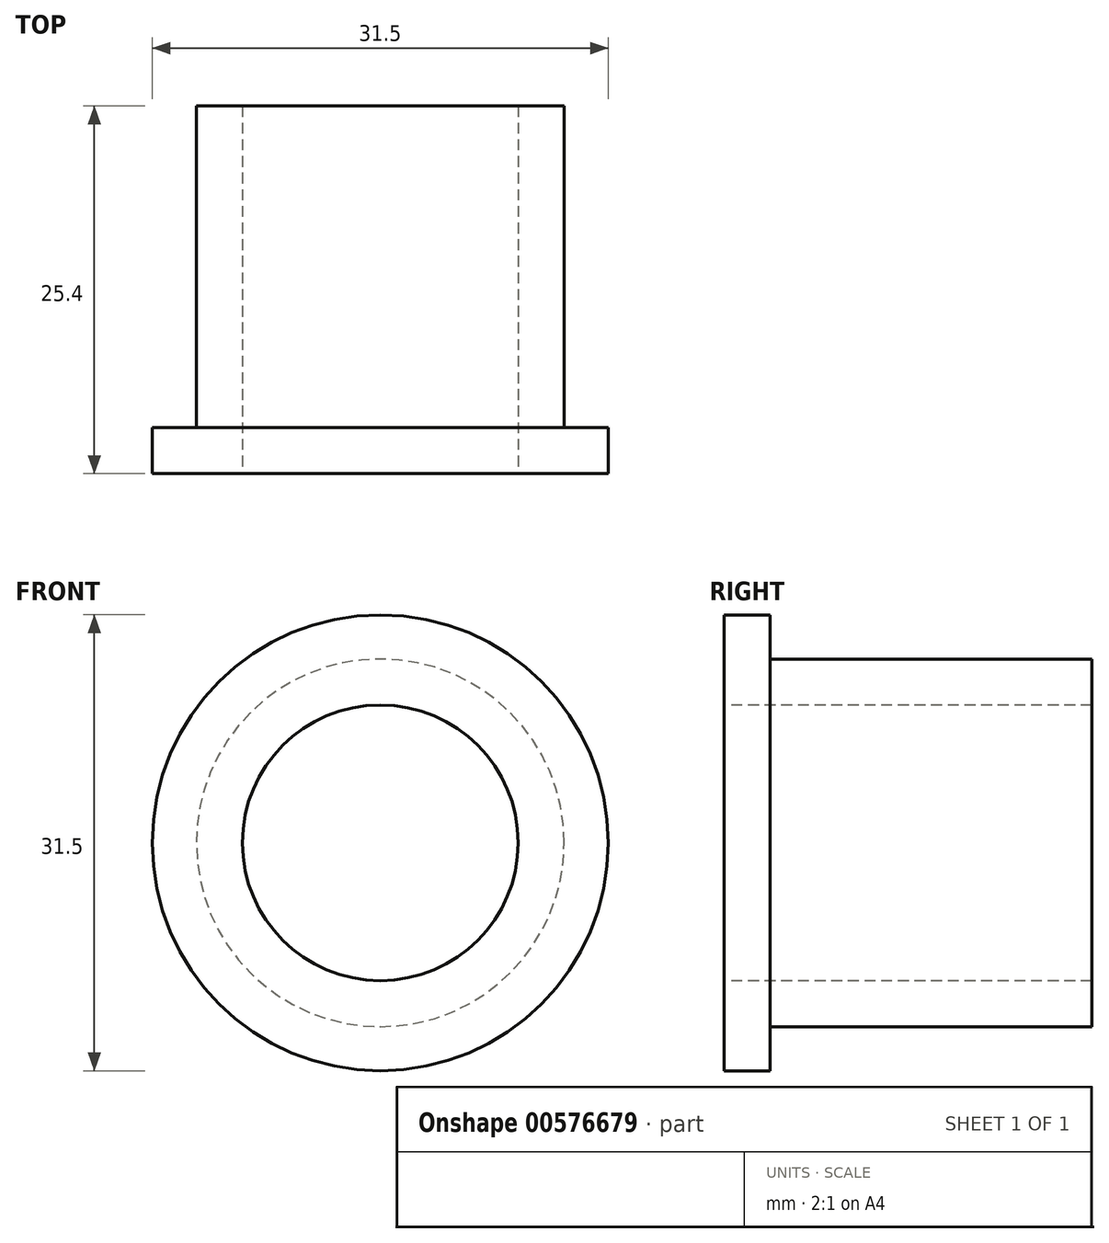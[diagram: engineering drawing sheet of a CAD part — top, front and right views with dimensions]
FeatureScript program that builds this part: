
annotation { "Feature Type Name" : "Feature", "Feature Type Description" : "" }
export const myFeature = defineFeature(function(context is Context, id is Id, definition is map)
    precondition{}
    {
        {
            var Q0;
            Q0=qCreatedBy(makeId("Front.planeOp"),FACE);
            var sketch = newSketch(context, id + "F0", { "sketchPlane" : qUnion([Q0])});
            skCircle(sketch, "E0", {"center": v(0, 0) * mm, "radius": 15.75 * mm});
            skCircle(sketch, "E1", {"center": v(0, 0) * mm, "radius": 12.7 * mm});
            skSolve(sketch);
        }
        {
            var Q0;
            Q0=makeQuery(id+"F0.imprint","IMPRINT",FACE,{"disambiguationData":[TD([[makeQuery(id+"F0.imprint","IMPRINT",EDGE,{"derivedFrom":sQuery(id+"F0.wireOp",EDGE,"E0")}),1.0]])]});
            var Q1;
            Q1=makeQuery(id+"F0.imprint","IMPRINT",FACE,{"disambiguationData":[TD([[makeQuery(id+"F0.imprint","IMPRINT",EDGE,{"derivedFrom":sQuery(id+"F0.wireOp",EDGE,"E1")}),1.0]])]});
            extrude(context, id + "F1", {"entities" : qUnion([Q0, Q1]), "depth" : -3.17 * mm, "offsetDistance" : 25.4 * mm});
        }
        {
            var Q0;
            Q0=makeQuery(id+"F0.imprint","IMPRINT",FACE,{"disambiguationData":[TD([[makeQuery(id+"F0.imprint","IMPRINT",EDGE,{"derivedFrom":sQuery(id+"F0.wireOp",EDGE,"E1")}),1.0]])]});
            extrude(context, id + "F2", {"entities" : qUnion([Q0]), "operationType" : NewBodyOperationType.ADD, "depth" : -25.4 * mm, "offsetDistance" : 25.4 * mm});
        }
        {
            var Q0;
            Q0=sQuery(id+"F0.wireOp",VERTEX,"E0.center");
            var Q1;
            Q1=makeQuery(id+"F1.opExtrude","SWEPT_BODY",BODY,{"disambiguationData":[OSD([sQuery(id+"F0.wireOp",EDGE,"E0")])]});
            hole(context, id + "F3", {"style" : HoleStyle.SIMPLE, "endStyle" : HoleEndStyle.THROUGH, "holeDiameter" : 19.05 * mm, "majorDiameter" : 6.35 * mm, "isTappedThrough" : true, "tappedDepth" : 12.7 * mm, "tapClearance" : 3, "locations" : qUnion([Q0]), "scope" : qUnion([Q1])});
        }
    });
